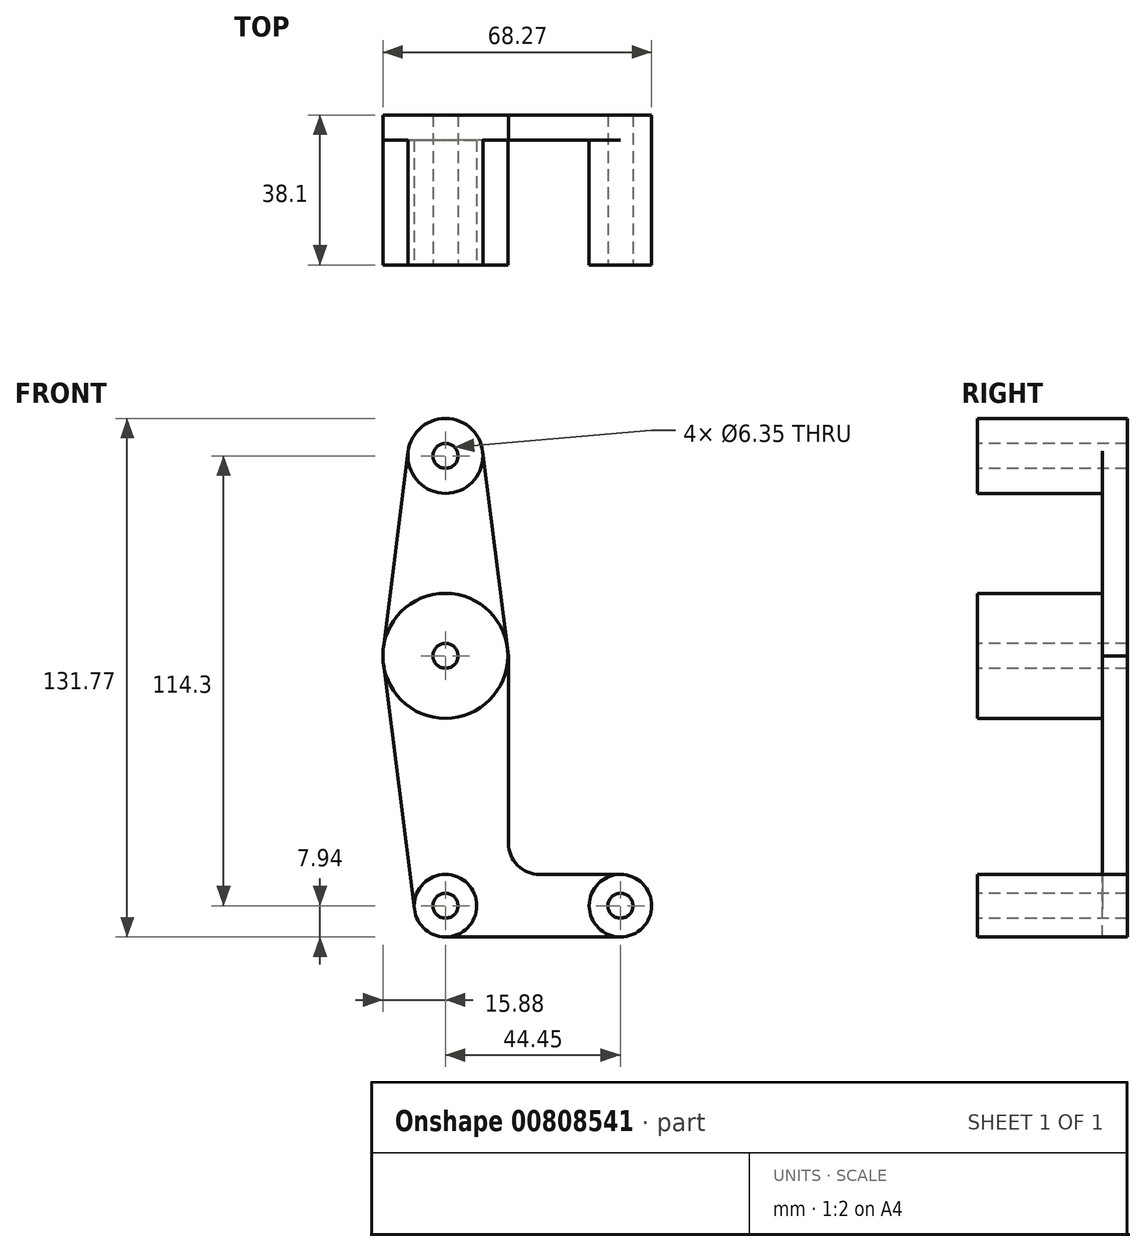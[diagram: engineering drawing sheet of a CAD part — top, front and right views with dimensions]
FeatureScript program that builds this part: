
annotation { "Feature Type Name" : "Feature", "Feature Type Description" : "" }
export const myFeature = defineFeature(function(context is Context, id is Id, definition is map)
    precondition{}
    {
        {
            var Q0;
            Q0=qCreatedBy(makeId("Front.planeOp"),FACE);
            var sketch = newSketch(context, id + "F0", { "sketchPlane" : qUnion([Q0])});
            skCircle(sketch, "E0", {"center": v(0, 0) * mm, "radius": 15.88 * mm});
            skCircle(sketch, "E1", {"center": v(0, 0) * mm, "radius": 3.18 * mm});
            skLineSegment(sketch, "E2", {"start": v(0, 0) * mm, "end": v(0, 50.8) * mm});
            skCircle(sketch, "E3", {"center": v(0, 50.8) * mm, "radius": 9.53 * mm});
            skCircle(sketch, "E4", {"center": v(0, 50.8) * mm, "radius": 3.18 * mm});
            skLineSegment(sketch, "E5", {"start": v(0, 0) * mm, "end": v(0, -63.5) * mm});
            skCircle(sketch, "E6", {"center": v(0, -63.5) * mm, "radius": 7.94 * mm});
            skCircle(sketch, "E7", {"center": v(0, -63.5) * mm, "radius": 3.18 * mm});
            skLineSegment(sketch, "E8", {"start": v(-9.45, 52) * mm, "end": v(-16, 0) * mm});
            skLineSegment(sketch, "E9", {"start": v(9.45, 52) * mm, "end": v(16, 0) * mm});
            skLineSegment(sketch, "E10", {"start": v(-16, 0) * mm, "end": v(-7.88, -64.5) * mm});
            skLineSegment(sketch, "E11", {"start": v(16, 0) * mm, "end": v(16, -47.61) * mm});
            skLineSegment(sketch, "E12", {"start": v(0, -63.5) * mm, "end": v(44.45, -63.5) * mm});
            skCircle(sketch, "E13", {"center": v(44.45, -63.5) * mm, "radius": 3.18 * mm});
            skCircle(sketch, "E14", {"center": v(44.45, -63.5) * mm, "radius": 7.94 * mm});
            skLineSegment(sketch, "E15", {"start": v(0, -55.56) * mm, "end": v(0, -55.56) * mm});
            skLineSegment(sketch, "E16", {"start": v(0, -71.44) * mm, "end": v(44.45, -71.44) * mm});
            skLineSegment(sketch, "E17.trimOffspring", {"start": v(23.95, -55.56) * mm, "end": v(44.45, -55.56) * mm});
            skPoint(sketch, "E18.orphan", {"position": v(7.94, -63.5) * mm});
            skPoint(sketch, "E19.visualSharp", {"position": v(16, -55.56) * mm});
            skArc(sketch, "E19.filletArc", {"start": v(16, -47.61) * mm, "mid": v(18.33, -53.23) * mm, "end": v(23.95, -55.56) * mm});
            skSolve(sketch);
        }
        {
            var Q0;
            {var subQ1=sQuery(id+"F0.wireOp",EDGE,"E0");var subQ7=makeQuery(id+"F0.imprint","INTERSECT",VERTEX,{"derivedFrom":[subQ1,sQuery(id+"F0.wireOp",EDGE,"E9")]});Q0=makeQuery(id+"F0.imprint","IMPRINT",FACE,{"disambiguationData":[TD([[makeQuery(id+"F0.imprint","IMPRINT",EDGE,{"disambiguationData":[TD([[subQ7,-1.0]])],"derivedFrom":subQ1}),1.0]])]});}
            var Q1;
            {var subQ5=sQuery(id+"F0.wireOp",EDGE,"E0");var subQ8=makeQuery(id+"F0.imprint","INTERSECT",VERTEX,{"derivedFrom":[subQ5,sQuery(id+"F0.wireOp",EDGE,"E8")]});Q1=makeQuery(id+"F0.imprint","IMPRINT",FACE,{"disambiguationData":[TD([[makeQuery(id+"F0.imprint","IMPRINT",EDGE,{"disambiguationData":[TD([[subQ8,1.0]])],"derivedFrom":subQ5}),1.0]])]});}
            var Q2;
            Q2=makeQuery(id+"F0.imprint","IMPRINT",FACE,{"disambiguationData":[TD([[makeQuery(id+"F0.imprint","IMPRINT",EDGE,{"derivedFrom":sQuery(id+"F0.wireOp",EDGE,"E4")}),-1.0]])]});
            var Q3;
            {var subQ0=sQuery(id+"F0.wireOp",EDGE,"E6");var subQ1=sQuery(id+"F0.wireOp",EDGE,"E5");var subQ2=makeQuery(id+"F0.imprint","INTERSECT",VERTEX,{"derivedFrom":[subQ1,subQ0]});Q3=makeQuery(id+"F0.imprint","IMPRINT",FACE,{"disambiguationData":[TD([[makeQuery(id+"F0.imprint","IMPRINT",EDGE,{"disambiguationData":[TD([[subQ2,-1.0]])],"derivedFrom":subQ1}),1.0]])]});}
            var Q4;
            {var subQ1=sQuery(id+"F0.wireOp",EDGE,"E5");var subQ5=sQuery(id+"F0.wireOp",EDGE,"E6");var subQ8=makeQuery(id+"F0.imprint","INTERSECT",VERTEX,{"derivedFrom":[subQ1,subQ5]});Q4=makeQuery(id+"F0.imprint","IMPRINT",FACE,{"disambiguationData":[TD([[makeQuery(id+"F0.imprint","IMPRINT",EDGE,{"disambiguationData":[TD([[subQ8,-1.0]])],"derivedFrom":subQ1}),-1.0]])]});}
            var Q5;
            Q5=makeQuery(id+"F0.imprint","IMPRINT",FACE,{"disambiguationData":[TD([[makeQuery(id+"F0.imprint","IMPRINT",EDGE,{"derivedFrom":sQuery(id+"F0.wireOp",EDGE,"E13")}),-1.0]])]});
            var Q6;
            {var subQ0=sQuery(id+"F0.wireOp",EDGE,"E8");var subQ1=sQuery(id+"F0.wireOp",EDGE,"E0");var subQ2=makeQuery(id+"F0.imprint","INTERSECT",VERTEX,{"derivedFrom":[subQ1,subQ0]});Q6=makeQuery(id+"F0.imprint","IMPRINT",FACE,{"disambiguationData":[TD([[makeQuery(id+"F0.imprint","IMPRINT",EDGE,{"disambiguationData":[TD([[subQ2,1.0]])],"derivedFrom":subQ1}),-1.0]])]});}
            var Q7;
            {var subQ0=sQuery(id+"F0.wireOp",EDGE,"E11");Q7=makeQuery(id+"F0.imprint","IMPRINT",FACE,{"disambiguationData":[TD([[makeQuery(id+"F0.imprint","IMPRINT",EDGE,{"derivedFrom":subQ0}),-1.0]])]});}
            var Q8;
            {var subQ0=sQuery(id+"F0.wireOp",EDGE,"E10");var subQ1=sQuery(id+"F0.wireOp",EDGE,"E0");var subQ2=makeQuery(id+"F0.imprint","INTERSECT",VERTEX,{"derivedFrom":[subQ1,subQ0]});Q8=makeQuery(id+"F0.imprint","IMPRINT",FACE,{"disambiguationData":[TD([[makeQuery(id+"F0.imprint","IMPRINT",EDGE,{"disambiguationData":[TD([[subQ2,-1.0]])],"derivedFrom":subQ1}),-1.0]])]});}
            var Q9;
            {var subQ0=sQuery(id+"F0.wireOp",EDGE,"E9");var subQ1=sQuery(id+"F0.wireOp",EDGE,"E0");var subQ2=makeQuery(id+"F0.imprint","INTERSECT",VERTEX,{"derivedFrom":[subQ1,subQ0]});Q9=makeQuery(id+"F0.imprint","IMPRINT",FACE,{"disambiguationData":[TD([[makeQuery(id+"F0.imprint","IMPRINT",EDGE,{"disambiguationData":[TD([[subQ2,-1.0]])],"derivedFrom":subQ1}),-1.0]])]});}
            var Q10;
            {var subQ0=sQuery(id+"F0.wireOp",EDGE,"E16");Q10=makeQuery(id+"F0.imprint","IMPRINT",FACE,{"disambiguationData":[TD([[makeQuery(id+"F0.imprint","IMPRINT",EDGE,{"derivedFrom":subQ0}),1.0]])]});}
            extrude(context, id + "F1", {"entities" : qUnion([Q0, Q1, Q2, Q3, Q4, Q5, Q6, Q7, Q8, Q9, Q10]), "oppositeDirection" : true, "depth" : 6.35 * mm, "offsetDistance" : 25.4 * mm});
        }
        {
            var Q0;
            {var subQ5=sQuery(id+"F0.wireOp",EDGE,"E0");var subQ8=makeQuery(id+"F0.imprint","INTERSECT",VERTEX,{"derivedFrom":[subQ5,sQuery(id+"F0.wireOp",EDGE,"E8")]});Q0=makeQuery(id+"F0.imprint","IMPRINT",FACE,{"disambiguationData":[TD([[makeQuery(id+"F0.imprint","IMPRINT",EDGE,{"disambiguationData":[TD([[subQ8,1.0]])],"derivedFrom":subQ5}),1.0]])]});}
            var Q1;
            {var subQ1=sQuery(id+"F0.wireOp",EDGE,"E0");var subQ7=makeQuery(id+"F0.imprint","INTERSECT",VERTEX,{"derivedFrom":[subQ1,sQuery(id+"F0.wireOp",EDGE,"E9")]});Q1=makeQuery(id+"F0.imprint","IMPRINT",FACE,{"disambiguationData":[TD([[makeQuery(id+"F0.imprint","IMPRINT",EDGE,{"disambiguationData":[TD([[subQ7,-1.0]])],"derivedFrom":subQ1}),1.0]])]});}
            var Q2;
            {var subQ0=sQuery(id+"F0.wireOp",EDGE,"E6");var subQ3=sQuery(id+"F0.wireOp",EDGE,"E5");var subQ4=makeQuery(id+"F0.imprint","INTERSECT",VERTEX,{"derivedFrom":[subQ3,subQ0]});Q2=makeQuery(id+"F0.imprint","IMPRINT",FACE,{"disambiguationData":[TD([[makeQuery(id+"F0.imprint","IMPRINT",EDGE,{"disambiguationData":[TD([[subQ4,-1.0]])],"derivedFrom":subQ3}),-1.0]])]});}
            var Q3;
            {var subQ0=sQuery(id+"F0.wireOp",EDGE,"E6");var subQ1=sQuery(id+"F0.wireOp",EDGE,"E5");var subQ2=makeQuery(id+"F0.imprint","INTERSECT",VERTEX,{"derivedFrom":[subQ1,subQ0]});Q3=makeQuery(id+"F0.imprint","IMPRINT",FACE,{"disambiguationData":[TD([[makeQuery(id+"F0.imprint","IMPRINT",EDGE,{"disambiguationData":[TD([[subQ2,-1.0]])],"derivedFrom":subQ1}),1.0]])]});}
            var Q4;
            Q4=makeQuery(id+"F0.imprint","IMPRINT",FACE,{"disambiguationData":[TD([[makeQuery(id+"F0.imprint","IMPRINT",EDGE,{"derivedFrom":sQuery(id+"F0.wireOp",EDGE,"E13")}),-1.0]])]});
            var Q5;
            Q5=makeQuery(id+"F0.imprint","IMPRINT",FACE,{"disambiguationData":[TD([[makeQuery(id+"F0.imprint","IMPRINT",EDGE,{"derivedFrom":sQuery(id+"F0.wireOp",EDGE,"E4")}),-1.0]])]});
            extrude(context, id + "F2", {"entities" : qUnion([Q0, Q1, Q2, Q3, Q4, Q5]), "operationType" : NewBodyOperationType.ADD, "depth" : 31.75 * mm, "offsetDistance" : 25.4 * mm});
        }
    });
